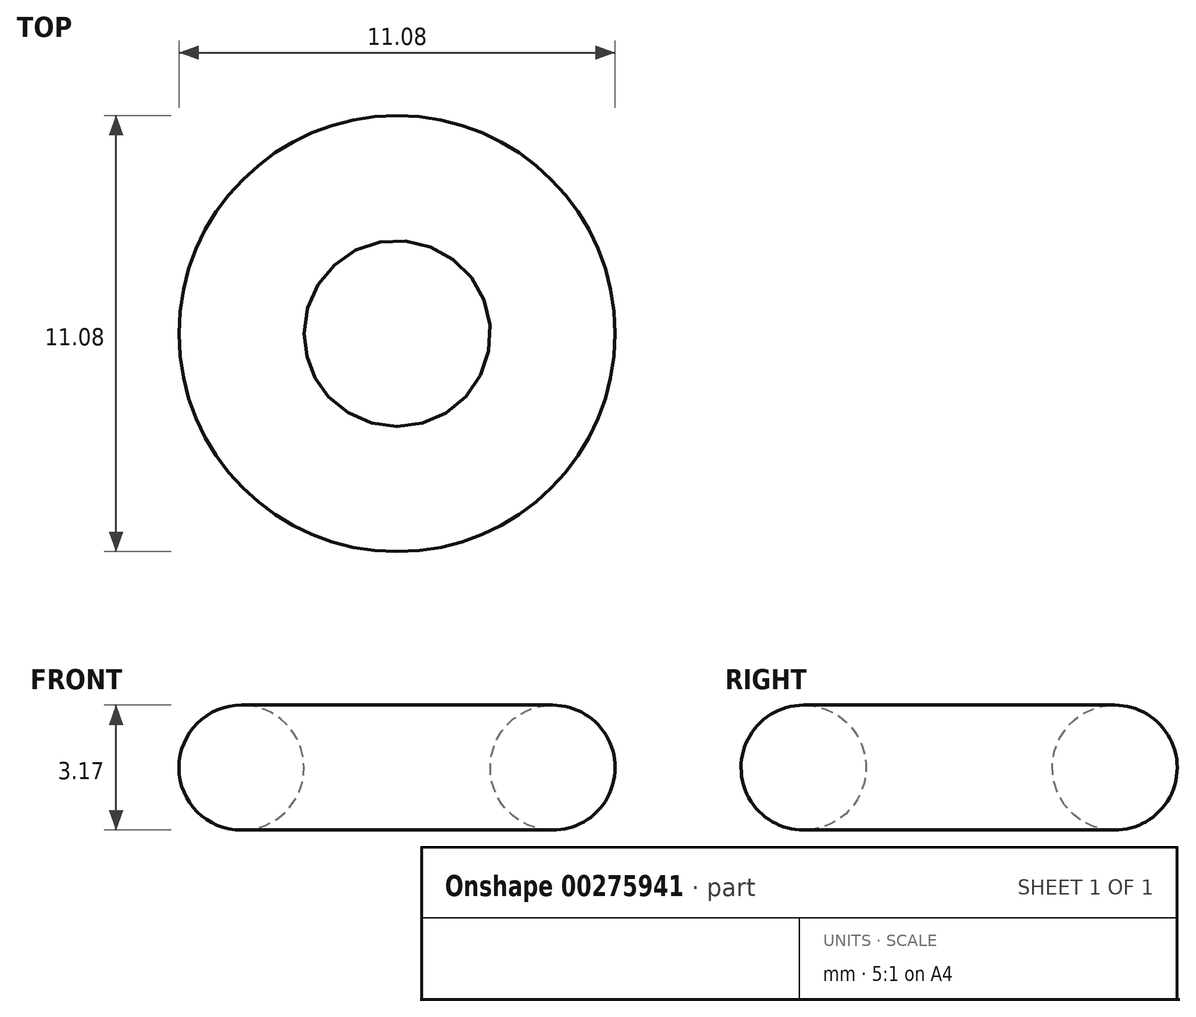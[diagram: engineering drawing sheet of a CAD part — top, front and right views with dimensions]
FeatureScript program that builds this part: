
annotation { "Feature Type Name" : "Feature", "Feature Type Description" : "" }
export const myFeature = defineFeature(function(context is Context, id is Id, definition is map)
    precondition{}
    {
        {
            var Q0;
            Q0=qCreatedBy(makeId("Front.planeOp"),FACE);
            var sketch = newSketch(context, id + "F0", { "sketchPlane" : qUnion([Q0])});
            skLineSegment(sketch, "E0", {"start": v(0, 18.94) * mm, "end": v(0, 59.4) * mm});
            skCircle(sketch, "E1", {"center": v(3.95, 42.3) * mm, "radius": 1.59 * mm});
            skSolve(sketch);
        }
        {
            var Q0;
            Q0=qSketchRegion(id+"F0",true);
            var Q1;
            Q1=sQuery(id+"F0.wireOp",EDGE,"E0");
            revolve(context, id + "F1", {"entities" : qUnion([Q0]), "axis" : qUnion([Q1]), "revolveType" : RevolveType.FULL});
        }
    });
